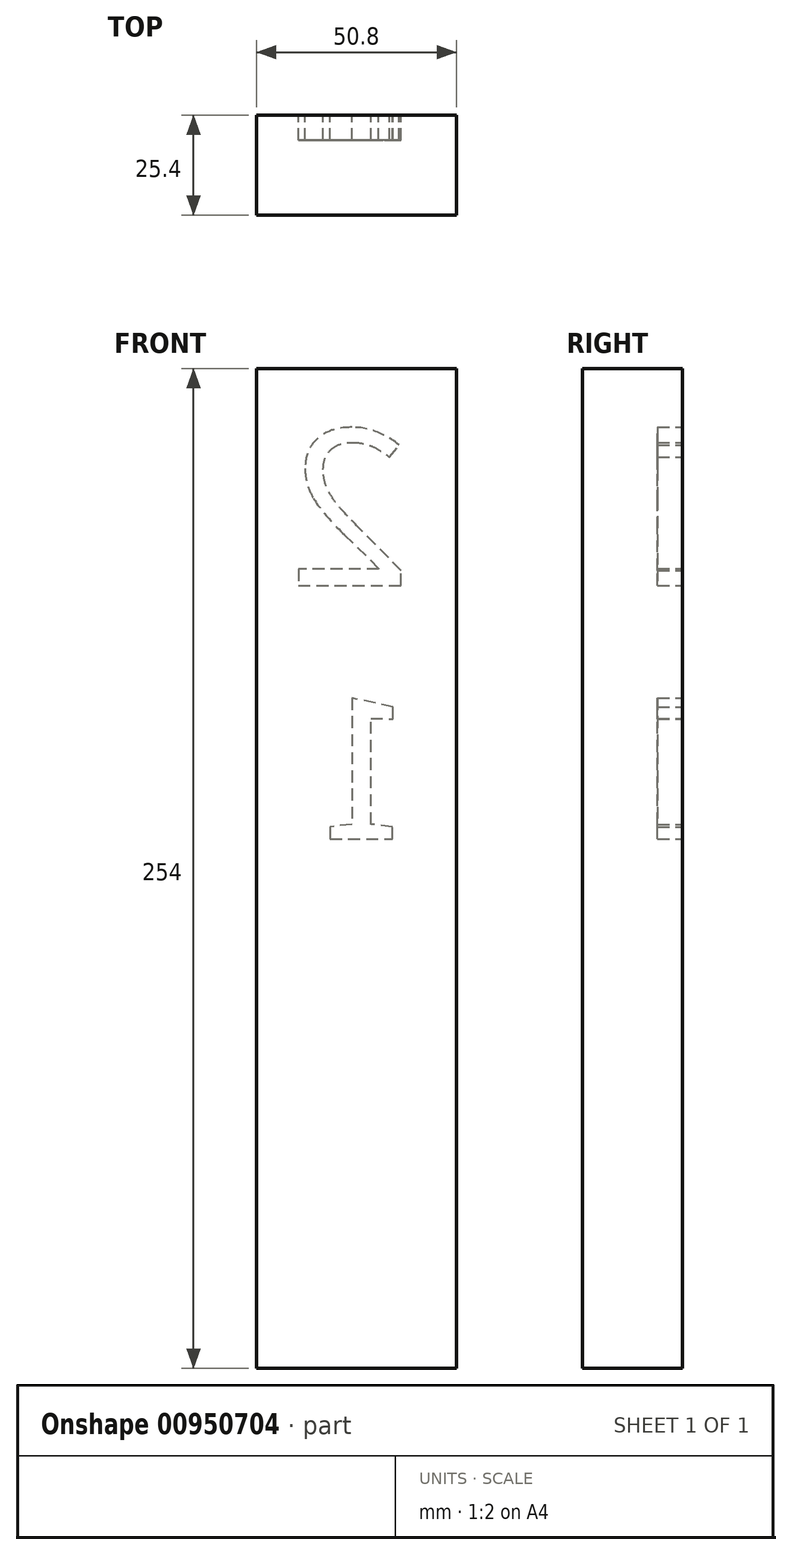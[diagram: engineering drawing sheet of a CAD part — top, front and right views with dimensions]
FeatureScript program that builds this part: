
annotation { "Feature Type Name" : "Feature", "Feature Type Description" : "" }
export const myFeature = defineFeature(function(context is Context, id is Id, definition is map)
    precondition{}
    {
        {
            var Q0;
            Q0=qCreatedBy(makeId("Top.planeOp"),FACE);
            var sketch = newSketch(context, id + "F0", { "sketchPlane" : qUnion([Q0])});
            skLineSegment(sketch, "E0.bottom", {"start": v(25.4, -12.7) * mm, "end": v(-25.4, -12.7) * mm});
            skLineSegment(sketch, "E0.top", {"start": v(25.4, 12.7) * mm, "end": v(-25.4, 12.7) * mm});
            skLineSegment(sketch, "E0.left", {"start": v(25.4, -12.7) * mm, "end": v(25.4, 12.7) * mm});
            skLineSegment(sketch, "E0.right", {"start": v(-25.4, -12.7) * mm, "end": v(-25.4, 12.7) * mm});
            skPoint(sketch, "E0.middle", {"position": v(0, 0) * mm});
            skSolve(sketch);
        }
        {
            var Q0;
            Q0=makeQuery(id+"F0.imprint","IMPRINT",FACE,{"disambiguationData":[TD([[makeQuery(id+"F0.imprint","IMPRINT",EDGE,{"derivedFrom":sQuery(id+"F0.wireOp",EDGE,"E0.bottom")}),-1.0]])]});
            extrude(context, id + "F1", {"entities" : qUnion([Q0]), "depth" : 254 * mm, "offsetDistance" : 25.4 * mm});
        }
        {
            var Q0;
            Q0=makeQuery(id+"F1.opExtrude","SWEPT_FACE",FACE,{"disambiguationData":[OSD([sQuery(id+"F0.wireOp",EDGE,"E0.top")])]});
            var sketch = newSketch(context, id + "F2", { "sketchPlane" : qUnion([Q0])});
            skText(sketch, "E1", { "text": "2", "fontName": "OpenSans-Regular.ttf"});
            const initialGuessF2  = {"E1": [-0.01403, 0.19888, 1, 0, 0.04]};
            skSetInitialGuess(sketch, initialGuessF2);
            skSolve(sketch);
        }
        {
            var Q0;
            Q0 = qSketchRegion(id + "F2", true);
            extrude(context, id + "F3", {"entities" : qUnion([Q0]), "operationType" : NewBodyOperationType.REMOVE, "oppositeDirection" : true, "depth" : 6.35 * mm, "offsetDistance" : 25.4 * mm});
        }
        {
            var Q0;
            Q0=makeQuery(id+"F1.opExtrude","SWEPT_FACE",FACE,{"disambiguationData":[OSD([sQuery(id+"F0.wireOp",EDGE,"E0.top")])]});
            var sketch = newSketch(context, id + "F4", { "sketchPlane" : qUnion([Q0])});
            skText(sketch, "E2", { "text": "1", "fontName": "RobotoSlab-Regular.ttf"});
            const initialGuessF4  = {"E2": [-0.01218, 0.13445, 1, 0, 0.0363]};
            skSetInitialGuess(sketch, initialGuessF4);
            skSolve(sketch);
        }
        {
            var Q0;
            Q0 = qSketchRegion(id + "F4", true);
            extrude(context, id + "F5", {"entities" : qUnion([Q0]), "operationType" : NewBodyOperationType.REMOVE, "oppositeDirection" : true, "depth" : 6.35 * mm, "offsetDistance" : 25.4 * mm});
        }
    });
